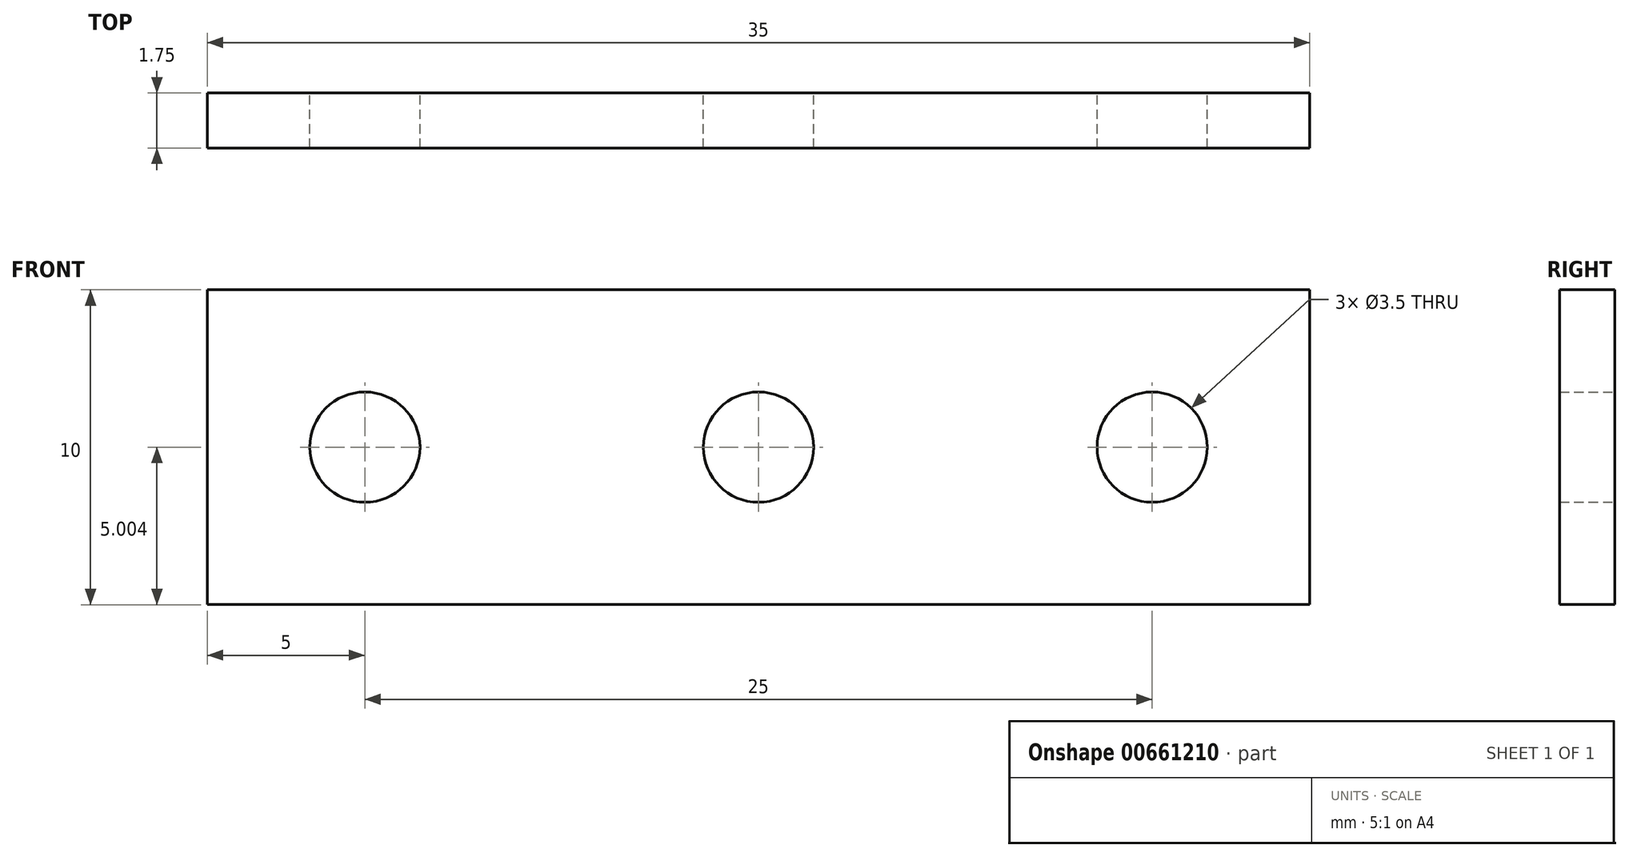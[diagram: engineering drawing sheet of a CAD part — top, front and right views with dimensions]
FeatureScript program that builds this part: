
annotation { "Feature Type Name" : "Feature", "Feature Type Description" : "" }
export const myFeature = defineFeature(function(context is Context, id is Id, definition is map)
    precondition{}
    {
        {
            var Q0;
            Q0=qCreatedBy(makeId("Front.planeOp"),FACE);
            var sketch = newSketch(context, id + "F0", { "sketchPlane" : qUnion([Q0])});
            skLineSegment(sketch, "E0", {"start": v(-17.5, 8.65) * mm, "end": v(17.5, 8.65) * mm});
            skLineSegment(sketch, "E1", {"start": v(17.5, 8.65) * mm, "end": v(17.5, -1.35) * mm});
            skLineSegment(sketch, "E2", {"start": v(17.5, -1.35) * mm, "end": v(-17.5, -1.35) * mm});
            skLineSegment(sketch, "E3", {"start": v(-17.5, -1.35) * mm, "end": v(-17.5, 8.65) * mm});
            skLineSegment(sketch, "E4", {"start": v(-17.5, -1.35) * mm, "end": v(-12.5, -1.35) * mm});
            skLineSegment(sketch, "E5", {"start": v(-12.5, -1.35) * mm, "end": v(-12.5, 3.65) * mm});
            skCircle(sketch, "E6", {"center": v(-12.5, 3.65) * mm, "radius": 1.75 * mm});
            skLineSegment(sketch, "E7", {"start": v(17.5, -1.35) * mm, "end": v(12.5, -1.35) * mm});
            skLineSegment(sketch, "E8", {"start": v(12.5, -1.35) * mm, "end": v(12.5, 3.65) * mm});
            skCircle(sketch, "E9", {"center": v(12.5, 3.65) * mm, "radius": 1.75 * mm});
            skLineSegment(sketch, "E10", {"start": v(12.5, 3.65) * mm, "end": v(0, 3.65) * mm});
            skCircle(sketch, "E11", {"center": v(0, 3.65) * mm, "radius": 1.75 * mm});
            skSolve(sketch);
        }
        {
            var Q0;
            Q0 = qSketchRegion(id + "F0", true);
            var Q1;
            Q1=makeQuery(id+"F0.imprint","IMPRINT",FACE,{"disambiguationData":[TD([[makeQuery(id+"F0.imprint","IMPRINT",EDGE,{"derivedFrom":sQuery(id+"F0.wireOp",EDGE,"E0")}),-1.0]])]});
            extrude(context, id + "F1", {"entities" : qUnion([Q0, Q1]), "depth" : 1.75 * mm, "offsetDistance" : 25.4 * mm});
        }
        {
            var Q0;
            Q0=makeQuery(id+"F1.opExtrude","CAP_FACE",FACE,{"disambiguationData":[OSD([sQuery(id+"F0.wireOp",EDGE,"E0"),sQuery(id+"F0.wireOp",EDGE,"E1"),sQuery(id+"F0.wireOp",EDGE,"E2"),sQuery(id+"F0.wireOp",EDGE,"E3"),sQuery(id+"F0.wireOp",EDGE,"E4"),sQuery(id+"F0.wireOp",EDGE,"E6"),sQuery(id+"F0.wireOp",EDGE,"E7"),sQuery(id+"F0.wireOp",EDGE,"E9"),sQuery(id+"F0.wireOp",EDGE,"E11")])],"isStart":false});
            extrude(context, id + "F2", {"entities" : qUnion([Q0]), "operationType" : NewBodyOperationType.ADD, "oppositeDirection" : true, "depth" : 1.75 * mm, "offsetDistance" : 25.4 * mm});
        }
    });
